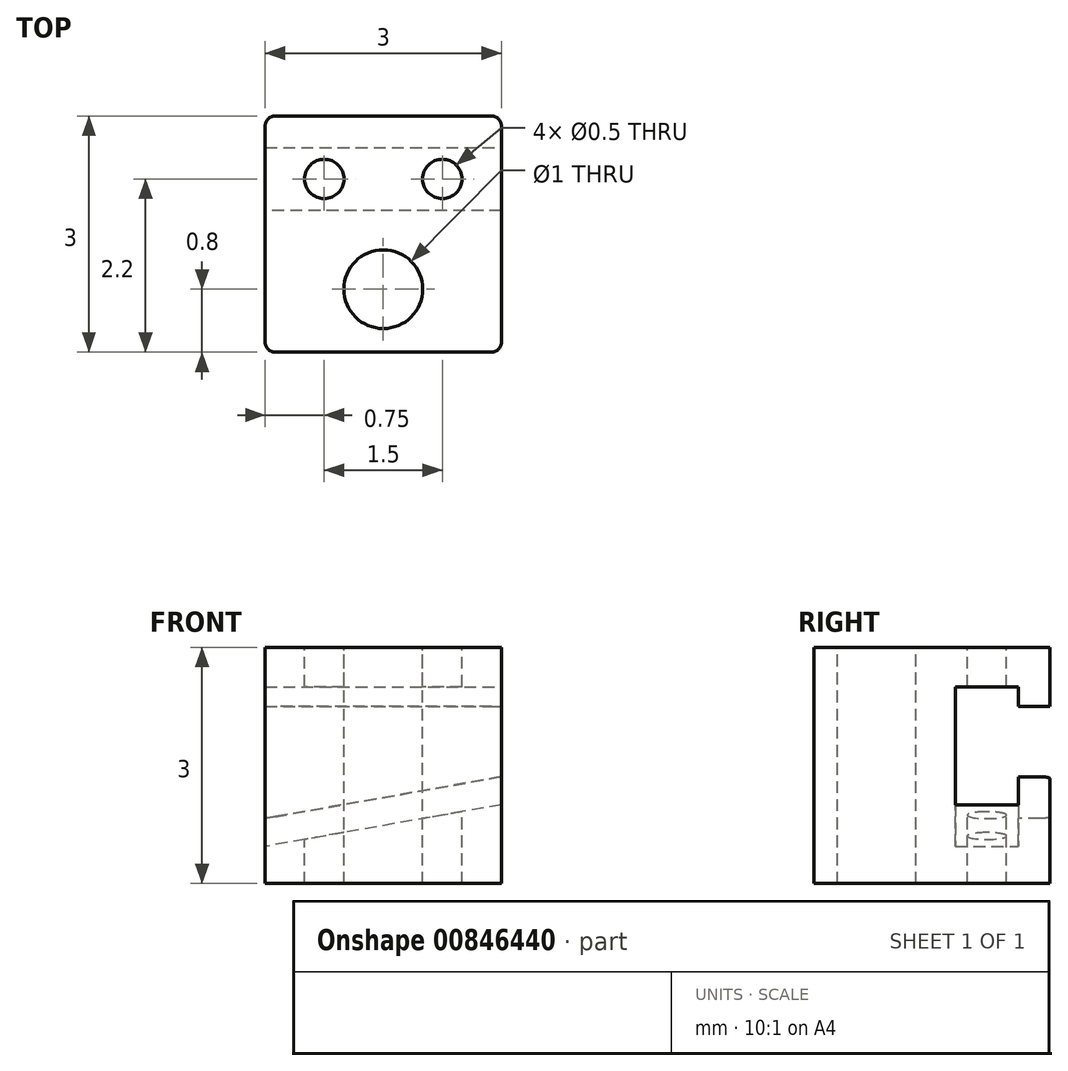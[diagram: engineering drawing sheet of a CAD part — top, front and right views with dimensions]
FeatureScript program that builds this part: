
annotation { "Feature Type Name" : "Feature", "Feature Type Description" : "" }
export const myFeature = defineFeature(function(context is Context, id is Id, definition is map)
    precondition{}
    {
        {
            var Q0;
            Q0=qCreatedBy(makeId("Top.planeOp"),FACE);
            var sketch = newSketch(context, id + "F0", { "sketchPlane" : qUnion([Q0])});
            skLineSegment(sketch, "E0.bottom", {"start": v(-1.5, 1.5) * mm, "end": v(1.5, 1.5) * mm});
            skLineSegment(sketch, "E0.top", {"start": v(-1.5, -1.5) * mm, "end": v(1.5, -1.5) * mm});
            skLineSegment(sketch, "E0.left", {"start": v(-1.5, 1.5) * mm, "end": v(-1.5, -1.5) * mm});
            skLineSegment(sketch, "E0.right", {"start": v(1.5, 1.5) * mm, "end": v(1.5, -1.5) * mm});
            skSolve(sketch);
        }
        {
            var Q0;
            Q0=makeQuery(id+"F0.imprint","IMPRINT",FACE,{"disambiguationData":[TD([[makeQuery(id+"F0.imprint","IMPRINT",EDGE,{"derivedFrom":sQuery(id+"F0.wireOp",EDGE,"E0.bottom")}),-1.0]])]});
            extrude(context, id + "F1", {"entities" : qUnion([Q0]), "depth" : 3 * mm, "offsetDistance" : 25 * mm});
        }
        {
            var Q0;
            Q0=makeQuery(id+"F1.opExtrude","CAP_FACE",FACE,{"disambiguationData":[OSD([sQuery(id+"F0.wireOp",EDGE,"E0.bottom"),sQuery(id+"F0.wireOp",EDGE,"E0.top"),sQuery(id+"F0.wireOp",EDGE,"E0.left"),sQuery(id+"F0.wireOp",EDGE,"E0.right")])],"isStart":false});
            var sketch = newSketch(context, id + "F2", { "sketchPlane" : qUnion([Q0])});
            skCircle(sketch, "E1", {"center": v(0, -0.7) * mm, "radius": 0.5 * mm});
            skSolve(sketch);
        }
        {
            var Q0;
            Q0=makeQuery(id+"F2.imprint","IMPRINT",FACE,{"disambiguationData":[TD([[makeQuery(id+"F2.imprint","IMPRINT",EDGE,{"derivedFrom":sQuery(id+"F2.wireOp",EDGE,"E1")}),1.0]])]});
            extrude(context, id + "F3", {"entities" : qUnion([Q0]), "operationType" : NewBodyOperationType.REMOVE, "oppositeDirection" : true, "depth" : 25 * mm, "offsetDistance" : 25 * mm});
        }
        {
            var Q0;
            Q0=makeQuery(id+"F1.opExtrude","SWEPT_FACE",FACE,{"disambiguationData":[OSD([sQuery(id+"F0.wireOp",EDGE,"E0.bottom")])]});
            cPlane(context, id + "F4", {"entities" : qUnion([Q0]), "cplaneType" : CPlaneType.OFFSET, "offset" : 0.4 * mm, "oppositeDirection" : true, "width" : 150 * mm, "height" : 150 * mm});
        }
        {
            var Q0;
            Q0=qCreatedBy(id+"F4.planeOp",FACE);
            var sketch = newSketch(context, id + "F5", { "sketchPlane" : qUnion([Q0])});
            skLineSegment(sketch, "E2", {"start": v(-1.5, 1) * mm, "end": v(1.5, 0.47) * mm});
            skLineSegment(sketch, "E3", {"start": v(1.5, 0.47) * mm, "end": v(1.5, 2.5) * mm});
            skLineSegment(sketch, "E4", {"start": v(1.5, 2.5) * mm, "end": v(-1.5, 2.5) * mm});
            skLineSegment(sketch, "E5", {"start": v(-1.5, 2.5) * mm, "end": v(-1.5, 1) * mm});
            skSolve(sketch);
        }
        {
            var Q0;
            Q0 = qSketchRegion(id + "F5", true);
            extrude(context, id + "F6", {"entities" : qUnion([Q0]), "operationType" : NewBodyOperationType.REMOVE, "oppositeDirection" : true, "depth" : 0.8 * mm, "offsetDistance" : 25 * mm});
        }
        {
            var Q0;
            Q0=qCreatedBy(id+"F4.planeOp",FACE);
            var sketch = newSketch(context, id + "F7", { "sketchPlane" : qUnion([Q0])});
            skLineSegment(sketch, "E6.0", {"start": v(-1.5, 1.36) * mm, "end": v(1.5, 0.83) * mm});
            skLineSegment(sketch, "E7.0", {"start": v(1.5, 2.25) * mm, "end": v(-1.5, 2.25) * mm});
            skLineSegment(sketch, "E8", {"start": v(-1.5, 2.25) * mm, "end": v(-1.5, 1.36) * mm});
            skLineSegment(sketch, "E9", {"start": v(1.5, 2.25) * mm, "end": v(1.5, 0.83) * mm});
            skSolve(sketch);
        }
        {
            var Q0;
            Q0 = qSketchRegion(id + "F7", true);
            extrude(context, id + "F8", {"entities" : qUnion([Q0]), "operationType" : NewBodyOperationType.REMOVE, "depth" : 1.05 * mm, "offsetDistance" : 25 * mm});
        }
        {
            var Q0;
            {var subQ0=sQuery(id+"F0.wireOp",EDGE,"E0.bottom");var subQ1=sQuery(id+"F0.wireOp",EDGE,"E0.right");Q0=makeQuery(id+"F8.boolean.opBoolean","SPLIT",EDGE,{"disambiguationData":[TD([makeQuery(id+"F8.opExtrude","SWEPT_FACE",FACE,{"disambiguationData":[OSD([sQuery(id+"F7.wireOp",EDGE,"E6.0")])]})])],"derivedFrom":makeQuery(id+"F1.opExtrude","SWEPT_EDGE",EDGE,{"disambiguationData":[OSD([subQ0,subQ1])]})});}
            var Q1;
            {var subQ0=sQuery(id+"F0.wireOp",EDGE,"E0.bottom");var subQ1=sQuery(id+"F0.wireOp",EDGE,"E0.right");Q1=makeQuery(id+"F8.boolean.opBoolean","SPLIT",EDGE,{"disambiguationData":[TD([makeQuery(id+"F8.opExtrude","SWEPT_FACE",FACE,{"disambiguationData":[OSD([sQuery(id+"F7.wireOp",EDGE,"E7.0")])]})])],"derivedFrom":makeQuery(id+"F1.opExtrude","SWEPT_EDGE",EDGE,{"disambiguationData":[OSD([subQ0,subQ1])]})});}
            fillet(context, id + "F9", {"entities" : qUnion([Q0, Q1]), "radius" : 0.12 * mm, "tangentPropagation" : true, "allowEdgeOverflow" : false});
        }
        {
            var Q0;
            {var subQ0=sQuery(id+"F0.wireOp",EDGE,"E0.bottom");var subQ1=sQuery(id+"F0.wireOp",EDGE,"E0.left");Q0=makeQuery(id+"F8.boolean.opBoolean","SPLIT",EDGE,{"disambiguationData":[TD([makeQuery(id+"F8.opExtrude","SWEPT_FACE",FACE,{"disambiguationData":[OSD([sQuery(id+"F7.wireOp",EDGE,"E7.0")])]})])],"derivedFrom":makeQuery(id+"F1.opExtrude","SWEPT_EDGE",EDGE,{"disambiguationData":[OSD([subQ0,subQ1])]})});}
            var Q1;
            {var subQ0=sQuery(id+"F0.wireOp",EDGE,"E0.bottom");var subQ1=sQuery(id+"F0.wireOp",EDGE,"E0.left");Q1=makeQuery(id+"F8.boolean.opBoolean","SPLIT",EDGE,{"disambiguationData":[TD([makeQuery(id+"F8.opExtrude","SWEPT_FACE",FACE,{"disambiguationData":[OSD([sQuery(id+"F7.wireOp",EDGE,"E6.0")])]})])],"derivedFrom":makeQuery(id+"F1.opExtrude","SWEPT_EDGE",EDGE,{"disambiguationData":[OSD([subQ0,subQ1])]})});}
            var Q2;
            Q2=makeQuery(id+"F1.opExtrude","SWEPT_EDGE",EDGE,{"disambiguationData":[OSD([sQuery(id+"F0.wireOp",EDGE,"E0.top"),sQuery(id+"F0.wireOp",EDGE,"E0.left")])]});
            var Q3;
            Q3=makeQuery(id+"F1.opExtrude","SWEPT_EDGE",EDGE,{"disambiguationData":[OSD([sQuery(id+"F0.wireOp",EDGE,"E0.top"),sQuery(id+"F0.wireOp",EDGE,"E0.right")])]});
            fillet(context, id + "F10", {"entities" : qUnion([Q0, Q1, Q2, Q3]), "radius" : 0.12 * mm, "tangentPropagation" : true, "allowEdgeOverflow" : false});
        }
        {
            var Q0;
            Q0=makeQuery(id+"F1.opExtrude","CAP_FACE",FACE,{"disambiguationData":[OSD([sQuery(id+"F0.wireOp",EDGE,"E0.bottom"),sQuery(id+"F0.wireOp",EDGE,"E0.top"),sQuery(id+"F0.wireOp",EDGE,"E0.left"),sQuery(id+"F0.wireOp",EDGE,"E0.right")])],"isStart":false});
            var sketch = newSketch(context, id + "F11", { "sketchPlane" : qUnion([Q0])});
            skCircle(sketch, "E10", {"center": v(0.75, 0.7) * mm, "radius": 0.25 * mm});
            skCircle(sketch, "E11", {"center": v(-0.75, 0.7) * mm, "radius": 0.25 * mm});
            skSolve(sketch);
        }
        {
            var Q0;
            Q0 = qSketchRegion(id + "F11", true);
            extrude(context, id + "F12", {"entities" : qUnion([Q0]), "operationType" : NewBodyOperationType.REMOVE, "oppositeDirection" : true, "depth" : 25 * mm, "offsetDistance" : 25 * mm});
        }
    });
